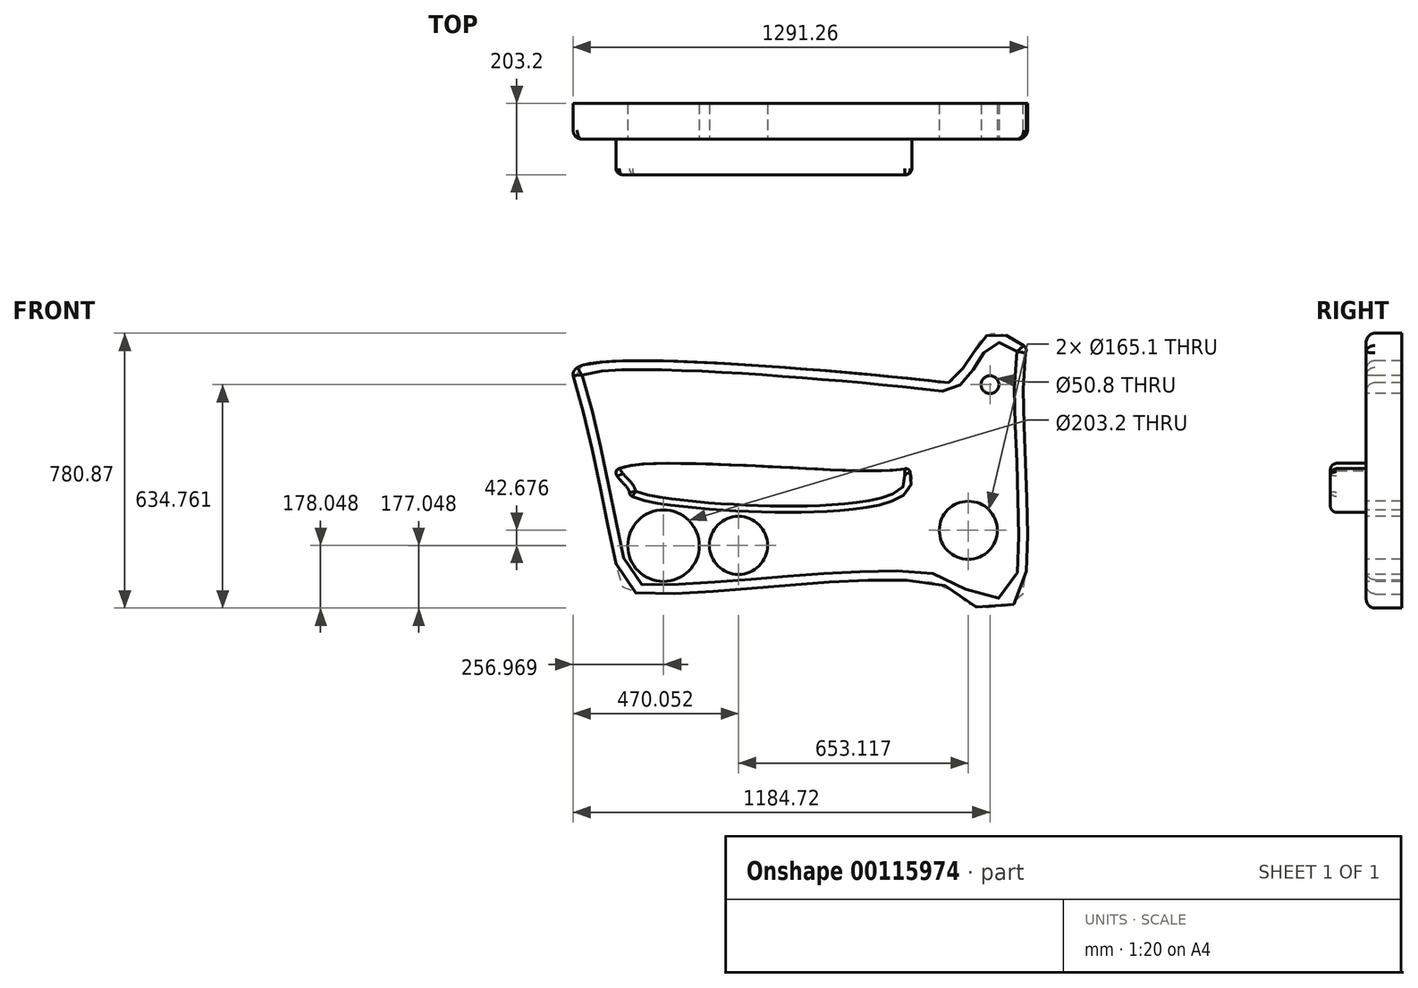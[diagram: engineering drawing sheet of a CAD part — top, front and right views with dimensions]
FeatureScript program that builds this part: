
annotation { "Feature Type Name" : "Feature", "Feature Type Description" : "" }
export const myFeature = defineFeature(function(context is Context, id is Id, definition is map)
    precondition{}
    {
        {
            var Q0;
            Q0=qCreatedBy(makeId("Front.planeOp"),FACE);
            var sketch = newSketch(context, id + "F0", { "sketchPlane" : qUnion([Q0])});
            skFitSpline(sketch, "E0", {"points": [v(-625.3, 298.66) * mm, v(390.7, 252.01) * mm, v(423.56, 254.12) * mm, v(478.76, 321.53) * mm, v(541.11, 389.8) * mm, v(632.96, 351.03) * mm, v(631.06, 315) * mm, v(630.43, -337.02) * mm, v(578.82, -385.69) * mm, v(474.96, -382.1) * mm, v(420.4, -333.86) * mm, v(-79.9, -329.23) * mm, v(-487.95, -344.82) * mm, v(-521.02, -300.15) * mm, v(-635.62, 212.62) * mm, v(-625.3, 298.66) * mm]});
            skSolve(sketch);
        }
        {
            var Q0;
            Q0=makeQuery(id+"F0.imprint","IMPRINT",FACE,{"disambiguationData":[TD([[makeQuery(id+"F0.imprint","IMPRINT",EDGE,{"derivedFrom":sQuery(id+"F0.wireOp",EDGE,"E0")}),-1.0]])]});
            extrude(context, id + "F11", {"entities" : qUnion([Q0]), "depth" : 101.6 * mm});
        }
        {
            var Q0;
            Q0=makeQuery(id+"F11.opExtrude","CAP_FACE",FACE,{"disambiguationData":[OSD([sQuery(id+"F0.wireOp",EDGE,"E0")])],"isStart":false});
            fillet(context, id + "F12", {"entities" : qUnion([Q0]), "radius" : 25.4 * mm, "tangentPropagation" : true, "allowEdgeOverflow" : false});
        }
        {
            var Q0;
            Q0=makeQuery(id+"F11.opExtrude","CAP_FACE",FACE,{"disambiguationData":[OSD([sQuery(id+"F0.wireOp",EDGE,"E0")])],"isStart":false});
            var sketch = newSketch(context, id + "F13", { "sketchPlane" : qUnion([Q0])});
            skCircle(sketch, "E1", {"center": v(533.63, 244.07) * mm, "radius": 25.4 * mm});
            skSolve(sketch);
        }
        {
            var Q0;
            Q0=sQuery(id+"F13.wireOp",VERTEX,"E1.center");
            var Q1;
            Q1=makeQuery(id+"F11.opExtrude","SWEPT_BODY",BODY,{"disambiguationData":[OSD([sQuery(id+"F0.wireOp",EDGE,"E0")])]});
            hole(context, id + "F1", {"style" : HoleStyle.SIMPLE, "endStyle" : HoleEndStyle.THROUGH, "holeDiameter" : 50.8 * mm, "locations" : qUnion([Q0]), "scope" : qUnion([Q1]), "isTappedThrough" : true});
        }
        {
            var Q0;
            Q0=makeQuery(id+"F11.opExtrude","CAP_FACE",FACE,{"disambiguationData":[OSD([sQuery(id+"F0.wireOp",EDGE,"E0")])],"isStart":false});
            var sketch = newSketch(context, id + "F2", { "sketchPlane" : qUnion([Q0])});
            skFitSpline(sketch, "E2", {"points": [v(427.16, 227) * mm, v(490.23, 96.26) * mm, v(607.22, 86.18) * mm], "startDerivative": vector(86.3, -308.22) * mm, "endDerivative": vector(451.11, 545.99) * mm});
            skSolve(sketch);
        }
        {
            var Q0;
            {var subQ0=sQuery(id+"F0.wireOp",EDGE,"E0");var subQ1=makeQuery(id+"F11.opExtrude","CAP_FACE",FACE,{"disambiguationData":[OSD([subQ0])],"isStart":false});var subQ2=makeQuery(id+"F11.opExtrude","CAP_EDGE",EDGE,{"disambiguationData":[OSD([subQ0])],"isStart":false});Q0=makeQuery(id+"F2.imprint","IMPRINT",FACE,{"disambiguationData":[TD([[makeQuery(id+"F2.imprint","IMPRINT",EDGE,{"derivedFrom":makeQuery(id+"F12.opFillet","BLEND_EDGE",EDGE,{"disambiguationData":[OD(0.0)],"blendedFrom":[subQ2,subQ1],"blendedInto":[subQ1]})}),1.0]])]});}
            var sketch = newSketch(context, id + "F3", { "sketchPlane" : qUnion([Q0])});
            skCircle(sketch, "E3", {"center": v(472.08, -169.97) * mm, "radius": 82.55 * mm});
            skSolve(sketch);
        }
        {
            var Q0;
            Q0=sQuery(id+"F3.wireOp",VERTEX,"E3.center");
            var Q1;
            Q1=makeQuery(id+"F11.opExtrude","SWEPT_BODY",BODY,{"disambiguationData":[OSD([sQuery(id+"F0.wireOp",EDGE,"E0")])]});
            hole(context, id + "F4", {"style" : HoleStyle.SIMPLE, "endStyle" : HoleEndStyle.THROUGH, "holeDiameter" : 165.1 * mm, "locations" : qUnion([Q0]), "scope" : qUnion([Q1]), "isTappedThrough" : true});
        }
        {
            var Q0;
            {var subQ0=sQuery(id+"F0.wireOp",EDGE,"E0");var subQ1=makeQuery(id+"F11.opExtrude","CAP_FACE",FACE,{"disambiguationData":[OSD([subQ0])],"isStart":false});var subQ2=makeQuery(id+"F11.opExtrude","CAP_EDGE",EDGE,{"disambiguationData":[OSD([subQ0])],"isStart":false});Q0=makeQuery(id+"F2.imprint","IMPRINT",FACE,{"disambiguationData":[TD([[makeQuery(id+"F2.imprint","IMPRINT",EDGE,{"derivedFrom":makeQuery(id+"F12.opFillet","BLEND_EDGE",EDGE,{"disambiguationData":[OD(0.0)],"blendedFrom":[subQ2,subQ1],"blendedInto":[subQ1]})}),1.0]])]});}
            var sketch = newSketch(context, id + "F5", { "sketchPlane" : qUnion([Q0])});
            skFitSpline(sketch, "E4", {"points": [v(305.01, 0) * mm, v(281.35, -74.61) * mm, v(-481.22, -75.22) * mm, v(-494.37, -52.57) * mm, v(-527.53, 0) * mm, v(249.2, 0) * mm, v(305.01, 0) * mm]});
            skSolve(sketch);
        }
        {
            var Q0;
            Q0 = qSketchRegion(id + "F5", true);
            extrude(context, id + "F6", {"entities" : qUnion([Q0]), "operationType" : NewBodyOperationType.ADD, "depth" : 101.6 * mm});
        }
        {
            var Q0;
            Q0=makeQuery(id+"F6.opExtrude","CAP_FACE",FACE,{"disambiguationData":[OSD([sQuery(id+"F5.wireOp",EDGE,"E4")])],"isStart":false});
            fillet(context, id + "F14", {"entities" : qUnion([Q0]), "radius" : 17.78 * mm, "tangentPropagation" : true, "allowEdgeOverflow" : false});
        }
        {
            var Q0;
            {var subQ0=sQuery(id+"F0.wireOp",EDGE,"E0");var subQ1=makeQuery(id+"F11.opExtrude","CAP_FACE",FACE,{"disambiguationData":[OSD([subQ0])],"isStart":false});var subQ2=makeQuery(id+"F11.opExtrude","CAP_EDGE",EDGE,{"disambiguationData":[OSD([subQ0])],"isStart":false});Q0=makeQuery(id+"F2.imprint","IMPRINT",FACE,{"disambiguationData":[TD([[makeQuery(id+"F2.imprint","IMPRINT",EDGE,{"derivedFrom":makeQuery(id+"F12.opFillet","BLEND_EDGE",EDGE,{"disambiguationData":[OD(0.0)],"blendedFrom":[subQ2,subQ1],"blendedInto":[subQ1]})}),1.0]])]});}
            var sketch = newSketch(context, id + "F7", { "sketchPlane" : qUnion([Q0])});
            skCircle(sketch, "E5", {"center": v(-394.12, -213.64) * mm, "radius": 101.6 * mm});
            skCircle(sketch, "E6", {"center": v(-181.04, -212.64) * mm, "radius": 82.55 * mm});
            skSolve(sketch);
        }
        {
            var Q0;
            Q0=sQuery(id+"F7.wireOp",VERTEX,"E5.center");
            var Q1;
            Q1=makeQuery(id+"F11.opExtrude","SWEPT_BODY",BODY,{"disambiguationData":[OSD([sQuery(id+"F0.wireOp",EDGE,"E0")])]});
            hole(context, id + "F8", {"style" : HoleStyle.SIMPLE, "endStyle" : HoleEndStyle.THROUGH, "holeDiameter" : 203.2 * mm, "startFromSketch" : true, "locations" : qUnion([Q0]), "scope" : qUnion([Q1]), "isTappedThrough" : true});
        }
        {
            var Q0;
            Q0=sQuery(id+"F7.wireOp",VERTEX,"E6.center");
            var Q1;
            Q1=makeQuery(id+"F11.opExtrude","SWEPT_BODY",BODY,{"disambiguationData":[OSD([sQuery(id+"F0.wireOp",EDGE,"E0")])]});
            hole(context, id + "F9", {"style" : HoleStyle.SIMPLE, "endStyle" : HoleEndStyle.THROUGH, "holeDiameter" : 165.1 * mm, "locations" : qUnion([Q0]), "scope" : qUnion([Q1]), "isTappedThrough" : true});
        }
    });
